# Revit family: Basin-Countertop-American_Standard-Aqualyn-047X_Series
name_source: partatom
category: Plumbing Fixtures
units: mm (PartAtom-declared; Revit-internal decimal feet)

## family parameters
Always vertical = No
Cut with Voids When Loaded = Yes
OmniClass Number = 23.45.05.14.14
OmniClass Title = Sinks/Lavatories
Part Type = Normal
Room Calculation Point = No
Round Connector Dimension = Use Radius
Shared = Yes
Work Plane-Based = Yes

## types (13) — shared parameters
ADA Compliant = Yes
ASME A112.19.2M = Yes
Assembly Code = D2010310
Basin Shape = Oval
Bowl Length = 10"
Bowl Width = 16"
CW Connection = Yes
CWFU = 1.5
Cold Water Connection Diameter = 3/8"
Cold Water Connection Radius = 3/16"
Default Elevation = 0"
Faucet Hole Distance = 8"
HW Connection = Yes
HW/CW Connection Depth = 11"
HWFU = 1.5
Height = 7"
Hot Water Connection Diameter = 0"
Hot Water Connection Radius = 3/16"
Installation Type = Counter Mounted
Length = 17 3/8"
Manufacturer = American Standard
Price = Prices may vary. Please consult Manufacturer Representative for most up-to-date price list.
Product Documentation Link = https://americanstandard.box.com
Product Page URL = https://www.americanstandard-us.com
Revised Date = 08/19/2021
Setback- Drain = 7 1/8"
Setback- Faucet Holes = 2 13/16"
Supplied With Cut-out Template = Yes
URL = http://www.americanstandard-us.com
Vent Connection = No
WFU = 2
Waste Connection = Yes
Waste Connection Depth = 12 3/4"
Waste Connection Diameter = 1 1/4"
Waste Connection Radius = 5/8"
Width = 20 3/8"

## per-type parameters (varying)
| type | 4"/8" Centreset | 4"/8" Holes | Centers | Description | Finish | Front Overflow | Left Hole | Left Hole (Hidden) | Left-Hand Hole | Less Overflow | Material | Overflow | Overflow Vis | Right Hole | Right Hole (Hidden) | Right-Hand Hole | Short Shank Soap/Lotion Dispenser Required |
| 0475.020.020 | Yes | 2" | 4" | Aqualyn® Drop-In Sink With 8-Inch Widespread | Vitreous China-American Standard-020-White | Yes | 1/4" | 1/8" | No | No | Vitreous China-American Standard-020-White | 2" | Yes | 1/4" | 1/8" | No | No |
| 0475.020.021 | Yes | 2" | 4" | Aqualyn® Drop-In Sink With 8-Inch Widespread | Vitreous China-American Standard-021-Bone | Yes | 1/4" | 1/8" | No | No | Vitreous China-American Standard-021-Bone | 2" | Yes | 1/4" | 1/8" | No | No |
| 0475.020.222 | Yes | 2" | 4" | Aqualyn® Drop-In Sink With 8-Inch Widespread | Vitreous China-American Standard-222-Linen | Yes | 1/4" | 1/8" | No | No | Vitreous China-American Standard-222-Linen | 2" | Yes | 1/4" | 1/8" | No | No |
| 0475.920.020 | Yes | 2" | 4" | Aqualyn® Countertop Sink With 8-Inch Centerset Less Overflow | Vitreous China-American Standard-020-White | No | 1/4" | 1/8" | No | Yes | Vitreous China-American Standard-020-White | 1/4" | No | 1/4" | 1/8" | No | Yes |
| 0476.028.020 | Yes | 2" | 2" | Aqualyn® Drop-In Sink With 4-Inch Centerset | Vitreous China-American Standard-020-White | Yes | 1/4" | 21/32" | No | No | Vitreous China-American Standard-020-White | 2" | Yes | 1/4" | 21/32" | No | No |
| 0476.028.021 | Yes | 2" | 2" | Aqualyn® Drop-In Sink With 4-Inch Centerset | Vitreous China-American Standard-021-Bone | Yes | 1/4" | 21/32" | No | No | Vitreous China-American Standard-021-Bone | 2" | Yes | 1/4" | 21/32" | No | No |
| 0476.028.222 | Yes | 2" | 2" | Aqualyn® Drop-In Sink With 4-Inch Centerset | Vitreous China-American Standard-222-Linen | Yes | 1/4" | 21/32" | No | No | Vitreous China-American Standard-222-Linen | 2" | Yes | 1/4" | 21/32" | No | No |
| 0476.037.020 | Yes | 2" | 2" | Aqualyn® Drop-In Sink With 4-Inch Centerset and Extra Right-Hand Hole | Vitreous China-American Standard-020-White | Yes | 1/4" | 21/32" | No | No | Vitreous China-American Standard-020-White | 2" | Yes | 2" | 21/32" | Yes | Yes |
| 0475.035.020 | Yes | 2" | 2" | Aqualyn® Drop-In Sink With 4-Inch Centerset and Extra Left-Hand Hole | Vitreous China-American Standard-020-White | Yes | 2" | 21/32" | Yes | No | Vitreous China-American Standard-020-White | 2" | Yes | 1/4" | 1/8" | No | Yes |
| 0476.928.020 | Yes | 2" | 2" | Aqualyn® Drop-In Sink With 4-Inch Centerset Less Overflow | Vitreous China-American Standard-020-White | No | 1/4" | 21/32" | No | Yes | Vitreous China-American Standard-020-White | 1/4" | No | 1/4" | 21/32" | No | Yes |
| 0475.047.020 | No | 1/4" | 2" | Aqualyn® Drop-In Sink With Center Hole Only | Vitreous China-American Standard-020-White | Yes | 1/4" | 21/32" | No | No | Vitreous China-American Standard-020-White | 2" | Yes | 1/4" | 21/32" | No | No |
| 0475.047.021 | No | 1/4" | 2" | Aqualyn® Drop-In Sink With Center Hole Only | Vitreous China-American Standard-021-Bone | Yes | 1/4" | 21/32" | No | No | Vitreous China-American Standard-021-Bone | 2" | Yes | 1/4" | 21/32" | No | No |
| 0475.047.222 | No | 1/4" | 2" | Aqualyn® Drop-In Sink With Center Hole Only | Vitreous China-American Standard-222-Linen | Yes | 1/4" | 21/32" | No | No | Vitreous China-American Standard-222-Linen | 2" | Yes | 1/4" | 21/32" | No | No |

note: column(s) folded — value = type name in every type: Model

## geometry (parser evidence)
native form markers: Sweep x1
no freeform markers — native parametric forms only
